# Revit family: SDCFC8X350
name_source: partatom
category: Structural Connections
revit_build: Autodesk Revit 2015 (Build: 20140606_1530(x64)
units: mm (PartAtom-declared; Revit-internal decimal feet)

## types (1)
- SDCFC8X350
    Default Elevation = 0 mm  [stored 0 ft]
    Density = 0.00 kg
    Description = 0015453411496193397454336628567759379235
    EPD = 0.09
    ETA / DoP = https://www.strongtie.eu
    Manufacturer = Simpson Strong-Tie
    Model = SDCFC8X350
    Model Disclaimer = Contact Simpson Strong-Tie Company  for more information
    Model ID = Simpson Strong-Tie
    Name = SDCFC8X350
    ObjectType = SDCFC8X350
    Product Material = E-coat®
    Product Type = 0015453411496193397454336628567759379235
    Reference = SDCFC8X350
    Technical datasheet = https://www.strongtie.eu
    URL = www.strongtie.eu
    UniClass Number = Wood screws
    UniClass Title = Joist hangers

note: [stored X ft] marks values corroborated as IEEE doubles in the binary element streams (Revit-internal decimal feet)

## geometry (parser evidence)
native form markers: Blend x24, Sweep x3
no freeform markers — native parametric forms only
